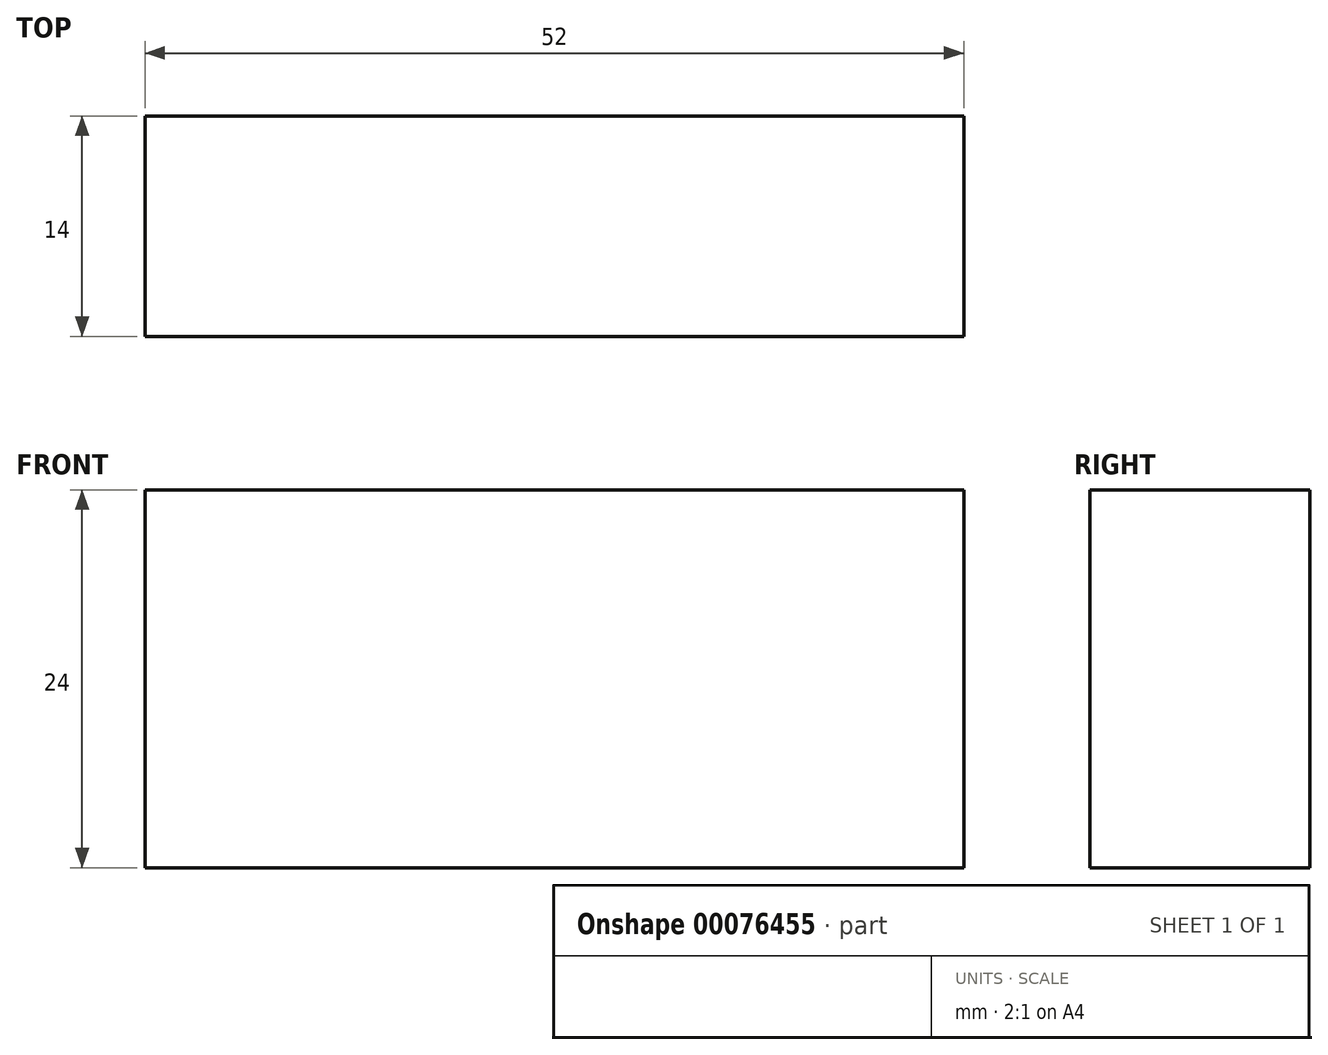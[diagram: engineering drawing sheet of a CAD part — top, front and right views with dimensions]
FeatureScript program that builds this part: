
annotation { "Feature Type Name" : "Feature", "Feature Type Description" : "" }
export const myFeature = defineFeature(function(context is Context, id is Id, definition is map)
    precondition{}
    {
        {
            var Q0;
            Q0=qCreatedBy(makeId("Front.planeOp"),FACE);
            var sketch = newSketch(context, id + "F0", { "sketchPlane" : qUnion([Q0])});
            skLineSegment(sketch, "E0.bottom", {"start": v(0, 24) * mm, "end": v(52, 24) * mm});
            skLineSegment(sketch, "E0.top", {"start": v(0, 0) * mm, "end": v(52, 0) * mm});
            skLineSegment(sketch, "E0.left", {"start": v(0, 24) * mm, "end": v(0, 0) * mm});
            skLineSegment(sketch, "E0.right", {"start": v(52, 24) * mm, "end": v(52, 0) * mm});
            skSolve(sketch);
        }
        {
            var Q0;
            Q0=makeQuery(id+"F0.imprint","IMPRINT",FACE,{"disambiguationData":[TD([[makeQuery(id+"F0.imprint","IMPRINT",EDGE,{"derivedFrom":sQuery(id+"F0.wireOp",EDGE,"E0.bottom")}),-1.0]])]});
            extrude(context, id + "F1", {"entities" : qUnion([Q0]), "oppositeDirection" : true, "depth" : 14 * mm});
        }
    });
